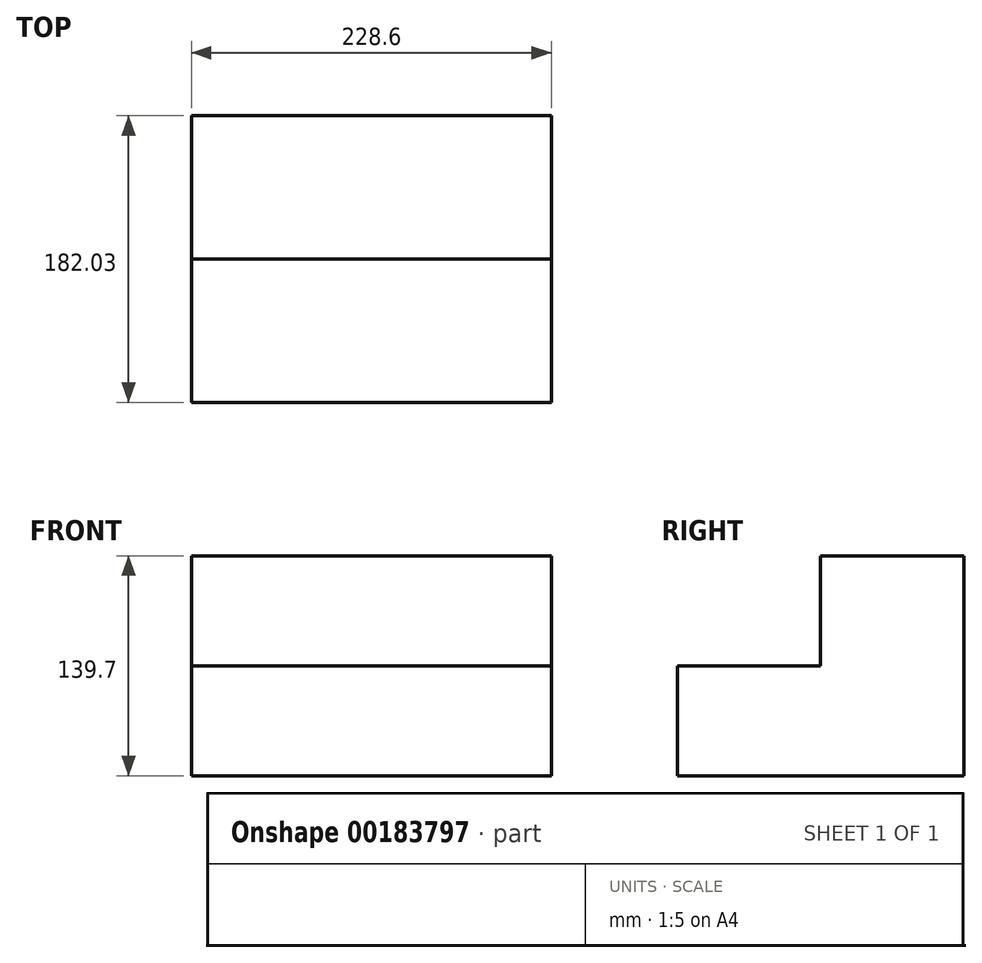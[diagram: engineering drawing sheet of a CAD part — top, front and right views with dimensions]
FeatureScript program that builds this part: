
annotation { "Feature Type Name" : "Feature", "Feature Type Description" : "" }
export const myFeature = defineFeature(function(context is Context, id is Id, definition is map)
    precondition{}
    {
        {
            var Q0;
            Q0=qCreatedBy(makeId("Right.planeOp"),FACE);
            var sketch = newSketch(context, id + "F0", { "sketchPlane" : qUnion([Q0])});
            skLineSegment(sketch, "E0.bottom", {"start": v(0, 0) * mm, "end": v(273.05, 0) * mm});
            skLineSegment(sketch, "E0.top", {"start": v(0, 228.6) * mm, "end": v(273.05, 228.6) * mm});
            skLineSegment(sketch, "E0.left", {"start": v(0, 0) * mm, "end": v(0, 228.6) * mm});
            skLineSegment(sketch, "E0.right", {"start": v(273.05, 0) * mm, "end": v(273.05, 228.6) * mm});
            skSolve(sketch);
        }
        {
            var Q0;
            Q0 = qSketchRegion(id + "F0", true);
            extrude(context, id + "F1", {"entities" : qUnion([Q0]), "oppositeDirection" : true, "depth" : 228.6 * mm});
        }
        {
            var Q0;
            Q0=makeQuery(id+"F1.opExtrude","CAP_FACE",FACE,{"disambiguationData":[OSD([sQuery(id+"F0.wireOp",EDGE,"E0.bottom"),sQuery(id+"F0.wireOp",EDGE,"E0.top"),sQuery(id+"F0.wireOp",EDGE,"E0.left"),sQuery(id+"F0.wireOp",EDGE,"E0.right")])],"isStart":true});
            var sketch = newSketch(context, id + "F2", { "sketchPlane" : qUnion([Q0])});
            skLineSegment(sketch, "E1", {"start": v(91.02, 228.6) * mm, "end": v(91.02, 69.85) * mm, "construction": true});
            skLineSegment(sketch, "E2", {"start": v(182.03, 228.6) * mm, "end": v(182.03, 139.7) * mm, "construction": true});
            skLineSegment(sketch, "E3", {"start": v(0, 190.24) * mm, "end": v(91.02, 190.24) * mm, "construction": true});
            skLineSegment(sketch, "E4", {"start": v(91.02, 190.24) * mm, "end": v(182.03, 190.24) * mm, "construction": true});
            skLineSegment(sketch, "E5", {"start": v(182.03, 190.24) * mm, "end": v(273.05, 190.24) * mm, "construction": true});
            skLineSegment(sketch, "E6", {"start": v(273.05, 139.7) * mm, "end": v(182.03, 139.7) * mm});
            skLineSegment(sketch, "E7", {"start": v(273.05, 69.85) * mm, "end": v(91.02, 69.85) * mm});
            skLineSegment(sketch, "E8", {"start": v(40.37, 139.7) * mm, "end": v(40.37, 69.85) * mm, "construction": true});
            skLineSegment(sketch, "E9", {"start": v(40.37, 69.85) * mm, "end": v(40.37, 0) * mm, "construction": true});
            skLineSegment(sketch, "E10", {"start": v(91.02, 69.85) * mm, "end": v(91.02, 0) * mm});
            skLineSegment(sketch, "E11", {"start": v(91.02, 69.85) * mm, "end": v(0, 69.85) * mm, "construction": true});
            skLineSegment(sketch, "E12", {"start": v(182.03, 139.7) * mm, "end": v(182.03, 0) * mm});
            skLineSegment(sketch, "E13", {"start": v(182.03, 139.7) * mm, "end": v(0, 139.7) * mm, "construction": true});
            skSolve(sketch);
        }
        {
            var Q0;
            {var subQ1=sQuery(id+"F2.wireOp",EDGE,"E6");Q0=makeQuery(id+"F2.imprint","IMPRINT",FACE,{"disambiguationData":[TD([[makeQuery(id+"F2.imprint","IMPRINT",EDGE,{"derivedFrom":subQ1}),-1.0]])]});}
            var Q1;
            Q1=makeQuery(id+"F1.opExtrude","CAP_FACE",FACE,{"disambiguationData":[OSD([sQuery(id+"F0.wireOp",EDGE,"E0.bottom"),sQuery(id+"F0.wireOp",EDGE,"E0.top"),sQuery(id+"F0.wireOp",EDGE,"E0.left"),sQuery(id+"F0.wireOp",EDGE,"E0.right")])],"isStart":false});
            extrude(context, id + "F3", {"entities" : qUnion([Q0]), "operationType" : NewBodyOperationType.REMOVE, "endBound" : BoundingType.UP_TO_SURFACE, "oppositeDirection" : true, "endBoundEntityFace" : qUnion([Q1]), "depth" : 25.4 * mm});
        }
    });
